# Revit family: Electronics_Commercial-Loudspeakers_Two-Way-Loudspeaker_CMX20T
name_source: partatom
category: Communication Devices
units: mm (PartAtom-declared; Revit-internal decimal feet)

## family parameters
Cut with Voids When Loaded = No
Host = Face
Maintain Annotation Orientation = No
OmniClass Number = 23.85.10.11.14.14.14
OmniClass Title = Loudspeakers
Part Type = Normal
Room Calculation Point = No
Round Connector Dimension = Use Diameter
Shared = No

## types (2) — shared parameters
100V transformer power taps in watts = 20 - 10 - 5
70V transformer power taps in watts = 20 - 10 - 5 - 2.5
Applicable in 100V = Yes
Applicable low impedance = Yes
Closest RAL colour (subject to deviations) = RAL9010 (W) / RAL9011 (BL)
Connector Description = Terminal strip; Low impedance 16 ohms, 70/100V operation
Cutout in mm = 223
Default Elevation = 4' - 0"
Depth = 0' - 3 1/2"
Description = CMX20T 8 Two-Way Loudspeaker, White
Diameter = 0' - 9 1/2"
Frequency response in Hz = 50 - 20K
Grille main material = Aluminium
IP rating = 54
Impedance in ohms = 16
Installation grip range in mm = 4 - 25
Loudspeaker system = 2-way
Low impedance RMS power in watts = 50
Low impedance dynamic power in watts = 100
Main construction material = ABS plastic
Manufacturer = Biamp
Max SPL 1m in dB = 108
Mounting system = 3 screws
Product Documentation Link = https://downloads.biamp.com
Product Page URL = https://www.biamp.com
Product data url = https://bimobject.com
SPL 1W/1m in dB = 88
Tweeter size in inch = 1
URL = https://www.biamp.com
Vertical dispersion angle 1000 Hz = 180°
Weight = 3.09 lb
Woofer cone material = Polypropylene
Woofer size in inch = 8

## per-type parameters (varying)
| type | Colour | Grill Material | Housing Material |
| CMX20T W | White | Biamp - Plastic - White(Grid) | Biamp - Plastic - White |
| CMX20T B | Black | Biamp - Plastic - Black(Grid) | Biamp - Plastic - Black |

note: column(s) folded — value = type name in every type: Model

## geometry (parser evidence)
native form markers: Sweep x1
no freeform markers — native parametric forms only
